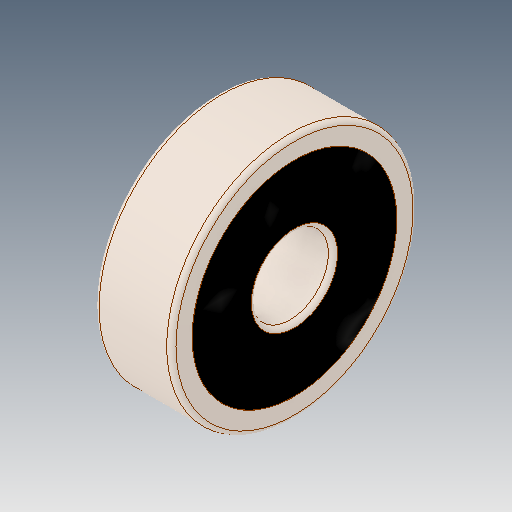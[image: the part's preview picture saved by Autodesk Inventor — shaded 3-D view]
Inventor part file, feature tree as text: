
AUTODESK INVENTOR PART (.ipt)
format: ipt  version: 2017 (Build 210142000, 142)  size: 2,075,136 bytes
history: mixed  units: mm
features: other x20, extrude x2, sketch x2, imported_body x1
ambient origin geometry x8: Origin, YZ Plane, XZ Plane, XY Plane, X Axis, Y Axis, Z Axis, Center Point
bodies: Solid1 (imported_parasolid), Solid2 (imported_parasolid), Solid3 (imported_parasolid), Solid4 (imported_parasolid), Solid5 (imported_parasolid), Solid6 (imported_parasolid), Solid7 (imported_parasolid), Solid8 (imported_parasolid), Solid9 (imported_parasolid), Solid10 (imported_parasolid), Solid11 (imported_parasolid), Solid12 (imported_parasolid), Solid13 (imported_parasolid), Solid14 (imported_parasolid), Solid15 (imported_parasolid), Solid16 (imported_parasolid), Solid17 (imported_parasolid), Solid18 (imported_parasolid), Solid19 (imported_parasolid), Solid20 (imported_parasolid)
feature tree (25):
  extrude  "Extrusion1"  Depth=0.5mm TaperAngle=0.0deg
  extrude  "Extrusion2"  [1 undecoded]
  sketch  "Sketch1"  dims[d0=0.5mm d1=0.0mm d2=0.5mm d3=0.0mm]
  sketch  "Sketch2"
  other  "SKF 625 Inner Race^SKF 625:1"
  other  "SKF 625 Outer Race^SKF 625:1"
  other  "SKF 625 Ball^SKF 625:1"
  other  "SKF 625 Ball^SKF 625:2"
  other  "SKF 625 Ball^SKF 625:3"
  other  "SKF 625 Ball^SKF 625:4"
  other  "SKF 625 Ball^SKF 625:5"
  other  "SKF 625 Ball^SKF 625:6"
  other  "SKF 625 Ball^SKF 625:7"
  other  "SKF 625 Ball^SKF 625:8"
  other  "SKF 625 Cage^SKF 625:1"
  other  "SKF 625 Cage^SKF 625:2"
  other  "SKF 625 Cage^SKF 625:3"
  other  "SKF 625 Cage^SKF 625:4"
  other  "SKF 625 Cage^SKF 625:5"
  other  "SKF 625 Cage^SKF 625:6"
  other  "SKF 625 Cage^SKF 625:7"
  other  "SKF 625 Cage^SKF 625:8"
  other  "SKF 625 Cage^SKF 625:9"
  other  "SKF 625 Cage^SKF 625:10"
  imported_body  NMx_Import_Brep_tag  [imported B-rep: ~49 faces, bbox_mm=[0.0, 10.2, 10.2]]
note: 1 required parameter value undecoded (feature->parameter linkage not recoverable at this tier; creation-order binding heuristic only, values carry confidence <= 0.55)
